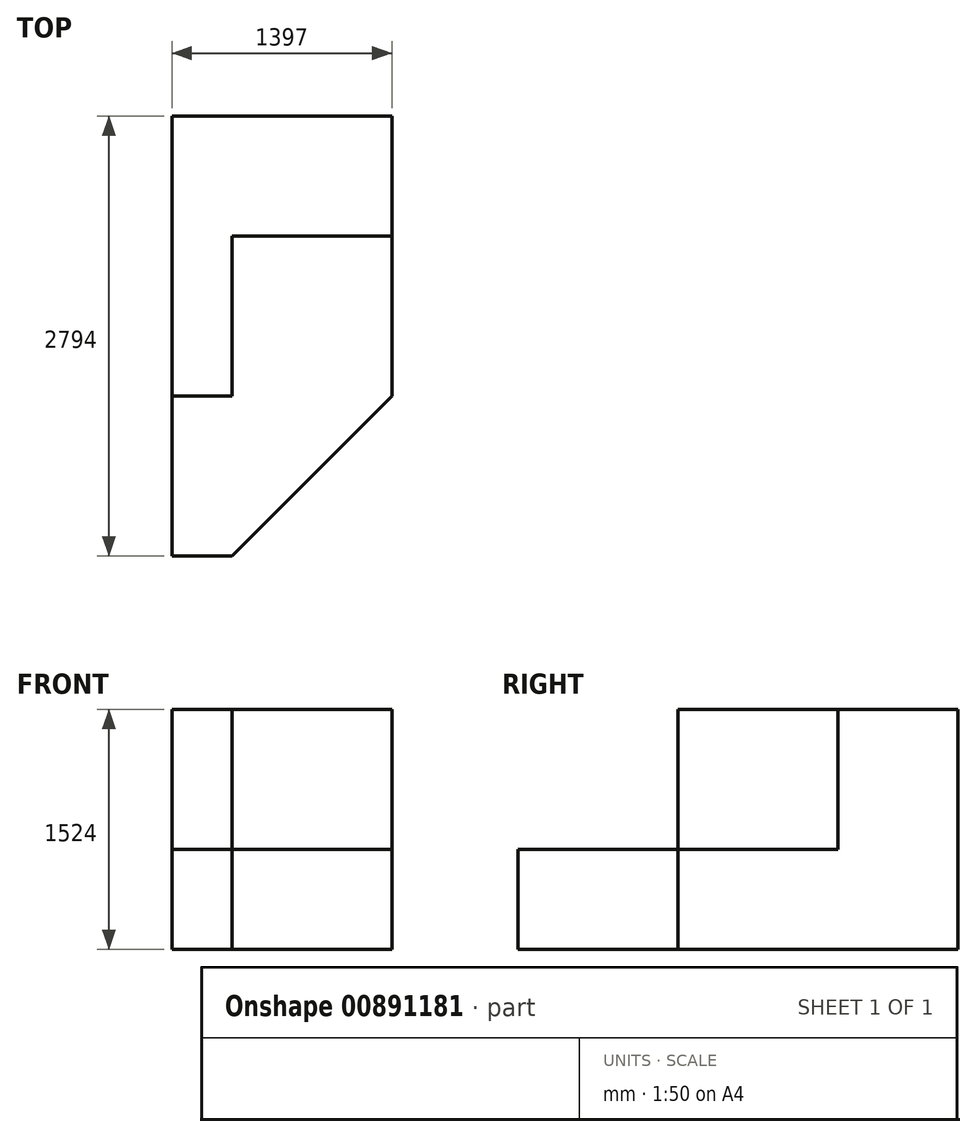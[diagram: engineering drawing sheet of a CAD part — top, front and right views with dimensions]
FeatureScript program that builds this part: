
annotation { "Feature Type Name" : "Feature", "Feature Type Description" : "" }
export const myFeature = defineFeature(function(context is Context, id is Id, definition is map)
    precondition{}
    {
        {
            var Q0;
            Q0=qCreatedBy(makeId("Right.planeOp"),FACE);
            var sketch = newSketch(context, id + "F0", { "sketchPlane" : qUnion([Q0])});
            skLineSegment(sketch, "E0.bottom", {"start": v(0, 0) * mm, "end": v(-2794, 0) * mm});
            skLineSegment(sketch, "E0.top", {"start": v(0, 1524) * mm, "end": v(-2794, 1524) * mm});
            skLineSegment(sketch, "E0.left", {"start": v(0, 0) * mm, "end": v(0, 1524) * mm});
            skLineSegment(sketch, "E0.right", {"start": v(-2794, 0) * mm, "end": v(-2794, 1524) * mm});
            skSolve(sketch);
        }
        {
            var Q0;
            Q0=makeQuery(id+"F0.imprint","IMPRINT",FACE,{"disambiguationData":[TD([[makeQuery(id+"F0.imprint","IMPRINT",EDGE,{"derivedFrom":sQuery(id+"F0.wireOp",EDGE,"E0.bottom")}),-1.0]])]});
            extrude(context, id + "F1", {"entities" : qUnion([Q0]), "depth" : 1397 * mm, "offsetDistance" : 25.4 * mm});
        }
        {
            var Q0;
            Q0=makeQuery(id+"F1.opExtrude","CAP_FACE",FACE,{"disambiguationData":[OSD([sQuery(id+"F0.wireOp",EDGE,"E0.bottom"),sQuery(id+"F0.wireOp",EDGE,"E0.top"),sQuery(id+"F0.wireOp",EDGE,"E0.left"),sQuery(id+"F0.wireOp",EDGE,"E0.right")])],"isStart":false});
            var sketch = newSketch(context, id + "F2", { "sketchPlane" : qUnion([Q0])});
            skLineSegment(sketch, "E1", {"start": v(0, 1524) * mm, "end": v(-762, 1524) * mm});
            skLineSegment(sketch, "E2", {"start": v(-762, 1524) * mm, "end": v(-762, 635) * mm});
            skLineSegment(sketch, "E3", {"start": v(-762, 635) * mm, "end": v(-1778, 635) * mm});
            skLineSegment(sketch, "E4", {"start": v(-1778, 635) * mm, "end": v(-1778, 1524) * mm});
            skSolve(sketch);
        }
        {
            var Q0;
            {var subQ0=sQuery(id+"F2.wireOp",EDGE,"E2");Q0=makeQuery(id+"F2.imprint","IMPRINT",FACE,{"disambiguationData":[TD([[makeQuery(id+"F2.imprint","IMPRINT",EDGE,{"derivedFrom":subQ0}),-1.0]])]});}
            extrude(context, id + "F3", {"entities" : qUnion([Q0]), "operationType" : NewBodyOperationType.REMOVE, "oppositeDirection" : true, "depth" : 2745.74 * mm, "offsetDistance" : 25.4 * mm});
        }
        {
            var Q0;
            Q0=makeQuery(id+"F1.opExtrude","CAP_FACE",FACE,{"disambiguationData":[OSD([sQuery(id+"F0.wireOp",EDGE,"E0.bottom"),sQuery(id+"F0.wireOp",EDGE,"E0.top"),sQuery(id+"F0.wireOp",EDGE,"E0.left"),sQuery(id+"F0.wireOp",EDGE,"E0.right")])],"isStart":false});
            var sketch = newSketch(context, id + "F4", { "sketchPlane" : qUnion([Q0])});
            skLineSegment(sketch, "E5", {"start": v(-1778, 635) * mm, "end": v(-2794, 635) * mm});
            skSolve(sketch);
        }
        {
            var Q0;
            {var subQ0=sQuery(id+"F4.wireOp",EDGE,"E5");Q0=makeQuery(id+"F4.imprint","IMPRINT",FACE,{"disambiguationData":[TD([[makeQuery(id+"F4.imprint","IMPRINT",EDGE,{"derivedFrom":subQ0}),-1.0]])]});}
            extrude(context, id + "F5", {"entities" : qUnion([Q0]), "operationType" : NewBodyOperationType.REMOVE, "oppositeDirection" : true, "depth" : 2430.78 * mm, "offsetDistance" : 25.4 * mm});
        }
        {
            var Q0;
            Q0=makeQuery(id+"F5.boolean.opBoolean","MERGE",FACE,{"derivedFrom":[makeQuery(id+"F3.boolean.opBoolean","COPY",FACE,{"derivedFrom":makeQuery(id+"F3.opExtrude","SWEPT_FACE",FACE,{"disambiguationData":[OSD([sQuery(id+"F2.wireOp",EDGE,"E3")])]})})],"fromTools":[makeQuery(id+"F5.opExtrude","SWEPT_FACE",FACE,{"disambiguationData":[OSD([sQuery(id+"F4.wireOp",EDGE,"E5")])]})]});
            var sketch = newSketch(context, id + "F6", { "sketchPlane" : qUnion([Q0])});
            skLineSegment(sketch, "E6", {"start": v(0, -2794) * mm, "end": v(381, -2794) * mm});
            skLineSegment(sketch, "E7", {"start": v(381, -2794) * mm, "end": v(1397, -2794) * mm});
            skLineSegment(sketch, "E8", {"start": v(1397, -2794) * mm, "end": v(1397, -762) * mm});
            skLineSegment(sketch, "E9", {"start": v(1397, -762) * mm, "end": v(1397, -1778) * mm});
            skLineSegment(sketch, "E10", {"start": v(1397, -1778) * mm, "end": v(381, -2794) * mm});
            skSolve(sketch);
        }
        {
            var Q0;
            Q0=makeQuery(id+"F6.imprint","IMPRINT",FACE,{"disambiguationData":[TD([[makeQuery(id+"F6.imprint","IMPRINT",EDGE,{"derivedFrom":sQuery(id+"F6.wireOp",EDGE,"E7")}),1.0]])]});
            extrude(context, id + "F7", {"entities" : qUnion([Q0]), "operationType" : NewBodyOperationType.REMOVE, "oppositeDirection" : true, "depth" : 1498.6 * mm, "offsetDistance" : 25.4 * mm});
        }
        {
            var Q0;
            Q0=makeQuery(id+"F1.opExtrude","CAP_FACE",FACE,{"disambiguationData":[OSD([sQuery(id+"F0.wireOp",EDGE,"E0.bottom"),sQuery(id+"F0.wireOp",EDGE,"E0.top"),sQuery(id+"F0.wireOp",EDGE,"E0.left"),sQuery(id+"F0.wireOp",EDGE,"E0.right")])],"isStart":true});
            var sketch = newSketch(context, id + "F8", { "sketchPlane" : qUnion([Q0])});
            skLineSegment(sketch, "E11.bottom", {"start": v(762, 1524) * mm, "end": v(1778, 1524) * mm});
            skLineSegment(sketch, "E11.top", {"start": v(762, 635) * mm, "end": v(1778, 635) * mm});
            skLineSegment(sketch, "E11.left", {"start": v(762, 1524) * mm, "end": v(762, 635) * mm});
            skLineSegment(sketch, "E11.right", {"start": v(1778, 1524) * mm, "end": v(1778, 635) * mm});
            skSolve(sketch);
        }
        {
            var Q0;
            Q0=makeQuery(id+"F8.imprint","IMPRINT",FACE,{"disambiguationData":[TD([[makeQuery(id+"F8.imprint","IMPRINT",EDGE,{"derivedFrom":sQuery(id+"F8.wireOp",EDGE,"E11.bottom")}),-1.0]])]});
            extrude(context, id + "F9", {"entities" : qUnion([Q0]), "operationType" : NewBodyOperationType.ADD, "oppositeDirection" : true, "depth" : 381 * mm, "offsetDistance" : 25.4 * mm});
        }
    });
